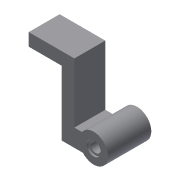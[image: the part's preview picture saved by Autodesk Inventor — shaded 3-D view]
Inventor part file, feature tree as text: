
AUTODESK INVENTOR PART (.ipt)
format: ipt  version: 2015 (Build 190159000, 159)  size: 139,264 bytes
history: native  units: in
note: dims shown in document units (in); Inventor stores cm internally (conversion verified against a paired STEP export)
features: extrude x5, sketch x5, mirror x3, reference x1, projected_geometry x1
ambient origin geometry x8: Origin, YZ Plane, XZ Plane, XY Plane, X Axis, Y Axis, Z Axis, Center Point
bodies: Solid1 (feature_tree)
feature tree (15):
  extrude  "Extrusion1"  Depth=0.9375in TaperAngle=0.0deg
  extrude  "Extrusion2"  Depth=0.4882in TaperAngle=0.0deg
  mirror  "Mirror1"
  extrude  "Extrusion3"  Depth=0.0591in TaperAngle=0.0deg
  extrude  "Extrusion4"  Depth=0.3831in
  mirror  "Mirror2"
  extrude  "Extrusion5"  [1 undecoded]
  mirror  "Mirror3"
  sketch  "Sketch1"  dims[d0=0.375in d1=0.0in d2=0.9375in d3=0.0in]
  reference  "Reference1"
  sketch  "Sketch2"  dims[d4=0.3125in d5=0.4882in d6=0.0in]
  sketch  "Sketch3"  dims[d7=0.4331in d8=0.0591in d9=0.0in]
  sketch  "Sketch4"  dims[d11=2.3455in d12=0.3831in]
  sketch  "Sketch7"  dims[d13=1.0in d14=0.0in]
  projected_geometry  "Projected Loop1"
note: 1 required parameter value undecoded (feature->parameter linkage not recoverable at this tier; creation-order binding heuristic only, values carry confidence <= 0.55)
